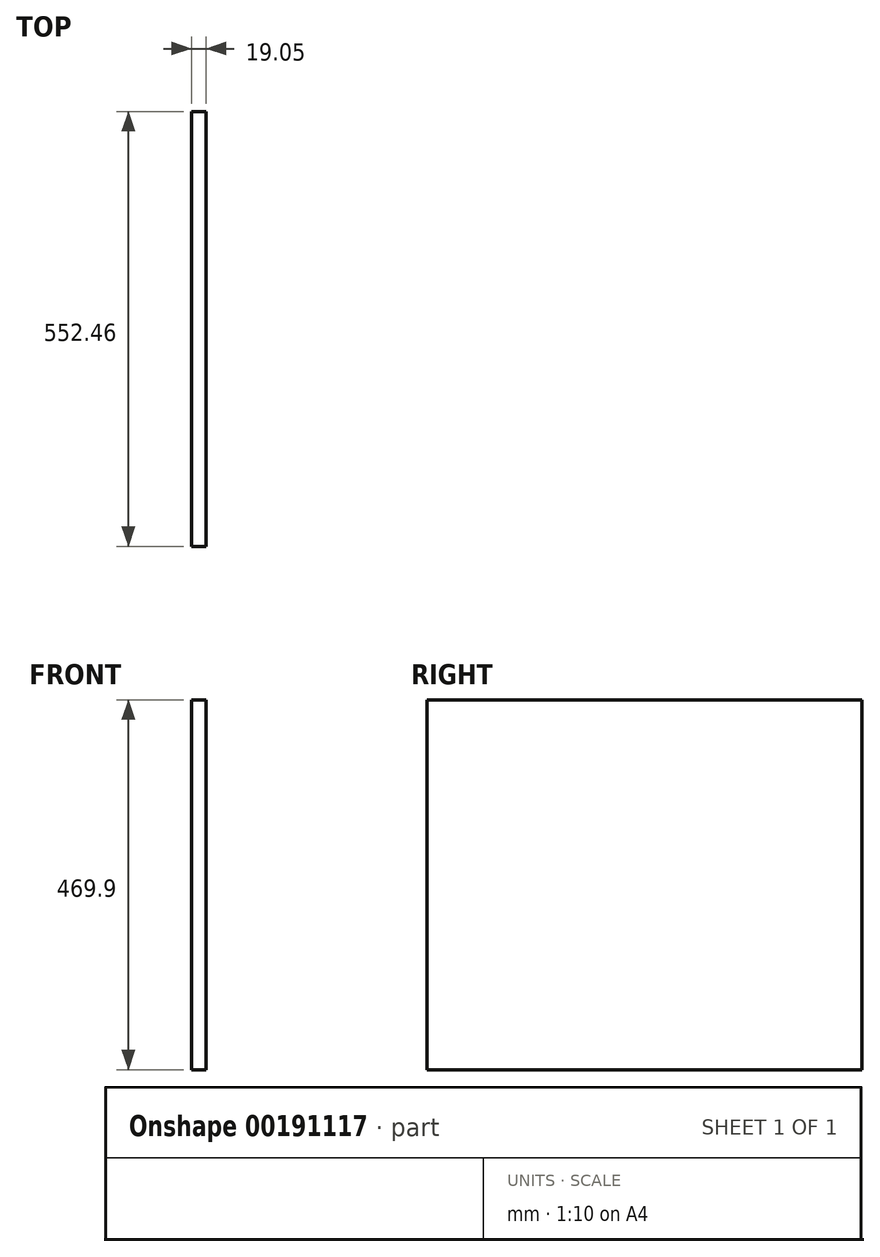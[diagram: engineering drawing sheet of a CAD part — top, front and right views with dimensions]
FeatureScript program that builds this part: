
annotation { "Feature Type Name" : "Feature", "Feature Type Description" : "" }
export const myFeature = defineFeature(function(context is Context, id is Id, definition is map)
    precondition{}
    {
        {
            var Q0;
            Q0=qCreatedBy(makeId("Right.planeOp"),FACE);
            var sketch = newSketch(context, id + "F0", { "sketchPlane" : qUnion([Q0])});
            skLineSegment(sketch, "E0.bottom", {"start": v(276.23, 234.95) * mm, "end": v(-276.23, 234.95) * mm});
            skLineSegment(sketch, "E0.top", {"start": v(276.23, -234.95) * mm, "end": v(-276.23, -234.95) * mm});
            skLineSegment(sketch, "E0.left", {"start": v(276.23, 234.95) * mm, "end": v(276.23, -234.95) * mm});
            skLineSegment(sketch, "E0.right", {"start": v(-276.23, 234.95) * mm, "end": v(-276.23, -234.95) * mm});
            skPoint(sketch, "E0.middle", {"position": v(0, 0) * mm});
            skSolve(sketch);
        }
        {
            var Q0;
            Q0 = qSketchRegion(id + "F0", true);
            extrude(context, id + "F1", {"entities" : qUnion([Q0]), "depth" : 19.05 * mm});
        }
    });
